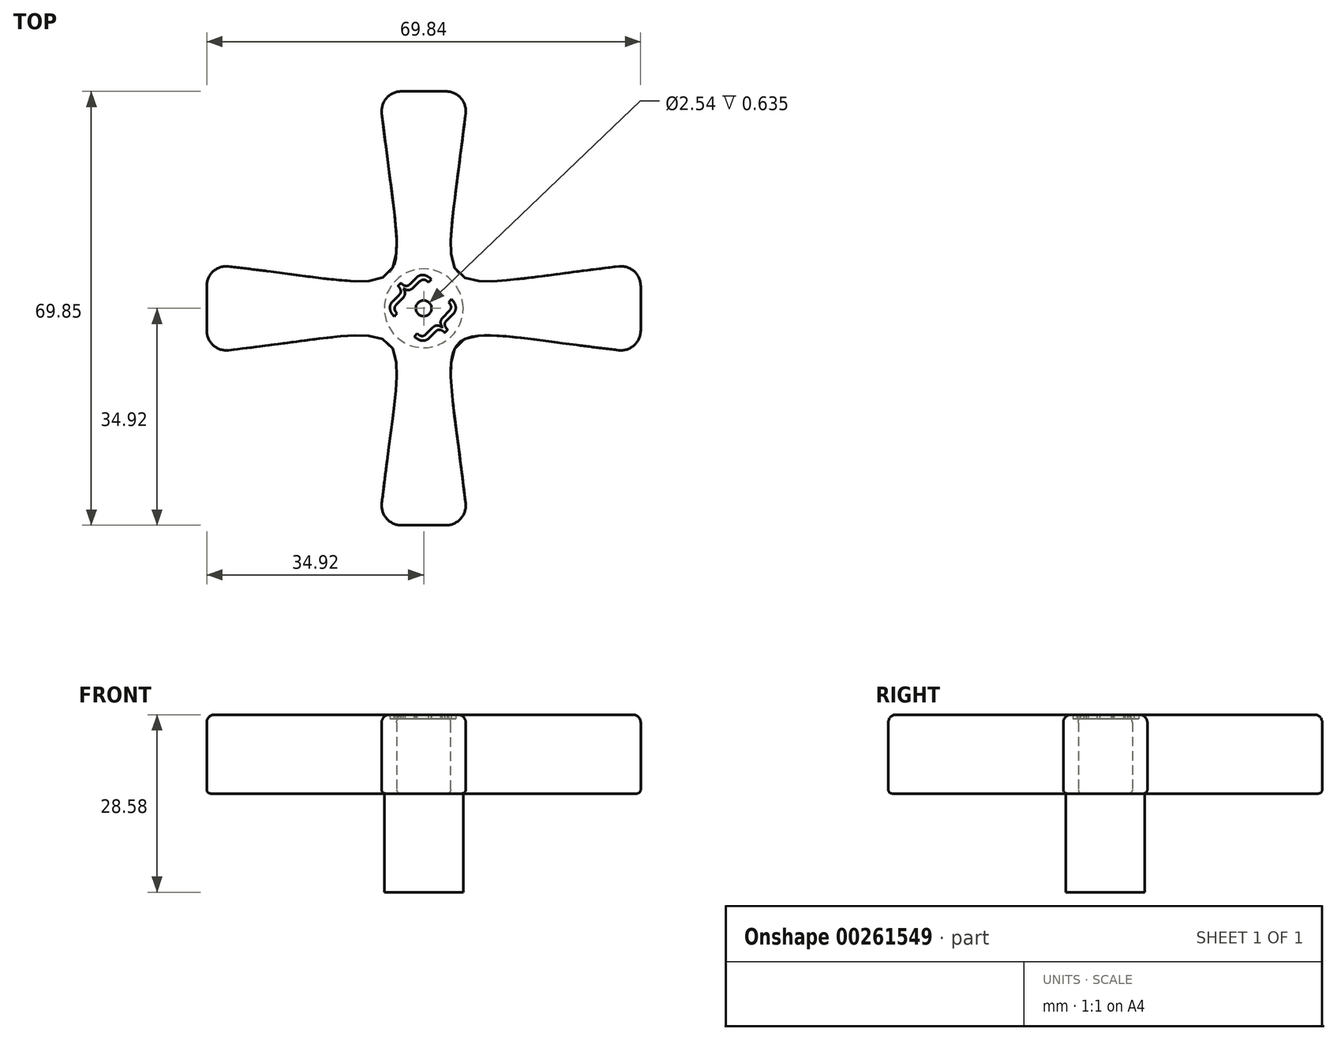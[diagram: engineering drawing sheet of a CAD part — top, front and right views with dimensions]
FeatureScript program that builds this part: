
annotation { "Feature Type Name" : "Feature", "Feature Type Description" : "" }
export const myFeature = defineFeature(function(context is Context, id is Id, definition is map)
    precondition{}
    {
        {
            var Q0;
            Q0=qCreatedBy(makeId("Top.planeOp"),FACE);
            var sketch = newSketch(context, id + "F0", { "sketchPlane" : qUnion([Q0])});
            skLineSegment(sketch, "E0", {"start": v(0, 0) * mm, "end": v(0, 34.93) * mm, "construction": true});
            skLineSegment(sketch, "E1", {"start": v(-34.92, 0) * mm, "end": v(0, 0) * mm, "construction": true});
            skLineSegment(sketch, "E2", {"start": v(34.93, 0) * mm, "end": v(0, 0) * mm, "construction": true});
            skLineSegment(sketch, "E3", {"start": v(0, -34.93) * mm, "end": v(0, 0) * mm, "construction": true});
            skLineSegment(sketch, "E4", {"start": v(-34.93, 7.14) * mm, "end": v(-34.93, -7.14) * mm});
            skLineSegment(sketch, "E5", {"start": v(-7.14, -34.93) * mm, "end": v(7.14, -34.93) * mm});
            skLineSegment(sketch, "E6", {"start": v(34.93, -7.14) * mm, "end": v(34.93, 7.14) * mm});
            skLineSegment(sketch, "E7", {"start": v(-7.14, 34.93) * mm, "end": v(7.14, 34.93) * mm});
            skCircle(sketch, "E8", {"center": v(0, 0) * mm, "radius": 15.88 * mm, "construction": true});
            skLineSegment(sketch, "E9", {"start": v(-15.88, 5.08) * mm, "end": v(-15.88, -5.08) * mm, "construction": true});
            skCircle(sketch, "E10", {"center": v(0, 0) * mm, "radius": 7.94 * mm, "construction": true});
            skLineSegment(sketch, "E11", {"start": v(-5.08, -15.88) * mm, "end": v(5.08, -15.88) * mm, "construction": true});
            skLineSegment(sketch, "E12.MirrorCS", {"start": v(0, 0) * mm, "end": v(0, -34.93) * mm, "construction": true});
            skLineSegment(sketch, "E13", {"start": v(-5.61, -5.61) * mm, "end": v(5.61, 5.61) * mm, "construction": true});
            skFitSpline(sketch, "E14", {"points": [v(-34.93, -7.14) * mm, v(-5.61, -5.61) * mm, v(-7.14, -34.93) * mm], "startDerivative": vector(114.3, 12.38) * mm, "endDerivative": vector(-12.38, -114.3) * mm});
            skFitSpline(sketch, "E15.MirrorCS", {"points": [v(34.93, -7.14) * mm, v(5.61, -5.61) * mm, v(7.14, -34.93) * mm], "startDerivative": vector(-114.3, 12.38) * mm, "endDerivative": vector(12.38, -114.3) * mm});
            skFitSpline(sketch, "E16.MirrorCS", {"points": [v(-34.93, 7.14) * mm, v(-5.61, 5.61) * mm, v(-7.14, 34.93) * mm], "startDerivative": vector(114.3, -12.38) * mm, "endDerivative": vector(-12.38, 114.3) * mm});
            skFitSpline(sketch, "E17.MirrorCS", {"points": [v(34.93, 7.14) * mm, v(5.61, 5.61) * mm, v(7.14, 34.93) * mm], "startDerivative": vector(-114.3, -12.38) * mm, "endDerivative": vector(12.38, 114.3) * mm});
            skSolve(sketch);
        }
        {
            var Q0;
            Q0=qSketchRegion(id+"F0",true);
            extrude(context, id + "F1", {"entities" : qUnion([Q0]), "depth" : 12.7 * mm});
        }
        {
            var Q0;
            Q0=makeQuery(id+"F1.opExtrude","CAP_FACE",FACE,{"disambiguationData":[OSD([sQuery(id+"F0.wireOp",EDGE,"E4"),sQuery(id+"F0.wireOp",EDGE,"E5"),sQuery(id+"F0.wireOp",EDGE,"E6"),sQuery(id+"F0.wireOp",EDGE,"E7"),sQuery(id+"F0.wireOp",EDGE,"E14"),sQuery(id+"F0.wireOp",EDGE,"E15.MirrorCS"),sQuery(id+"F0.wireOp",EDGE,"E16.MirrorCS"),sQuery(id+"F0.wireOp",EDGE,"E17.MirrorCS")])],"isStart":true});
            var sketch = newSketch(context, id + "F2", { "sketchPlane" : qUnion([Q0])});
            skCircle(sketch, "E18", {"center": v(0, 0) * mm, "radius": 6.35 * mm});
            skSolve(sketch);
        }
        {
            var Q0;
            Q0=qSketchRegion(id+"F2",true);
            extrude(context, id + "F3", {"entities" : qUnion([Q0]), "operationType" : NewBodyOperationType.ADD, "depth" : 15.88 * mm});
        }
        {
            var Q0;
            Q0=makeQuery(id+"FHBKJaG82kfliYF_1.boolean.opBoolean","MERGE",FACE,{"derivedFrom":[makeQuery(id+"F1.opExtrude","CAP_FACE",FACE,{"disambiguationData":[OSD([sQuery(id+"F0.wireOp",EDGE,"E4"),sQuery(id+"F0.wireOp",EDGE,"E5"),sQuery(id+"F0.wireOp",EDGE,"E6"),sQuery(id+"F0.wireOp",EDGE,"E7"),sQuery(id+"F0.wireOp",EDGE,"E14"),sQuery(id+"F0.wireOp",EDGE,"E15.MirrorCS"),sQuery(id+"F0.wireOp",EDGE,"E16.MirrorCS"),sQuery(id+"F0.wireOp",EDGE,"E17.MirrorCS")])],"isStart":false}),makeQuery(id+"FHBKJaG82kfliYF_1.opExtrude","CAP_FACE",FACE,{"disambiguationData":[OSD([sQuery(id+"FlcRGu9XOME26Uw_1.wireOp",EDGE,"4aeb7ee9-712b-4c87-8b6b-3736a43f95a2"),sQuery(id+"FlcRGu9XOME26Uw_1.wireOp",EDGE,"5124bdd7-5500-46ca-ada0-c6f18179f70a0.MirrorCS"),sQuery(id+"FlcRGu9XOME26Uw_1.wireOp",EDGE,"3c1a6850-1179-4b00-b570-ccdac5f7884b0.MirrorCS"),sQuery(id+"FlcRGu9XOME26Uw_1.wireOp",EDGE,"ff6566bc-f724-427d-8e95-42f8fa4ef3770.MirrorCS"),sQuery(id+"FlcRGu9XOME26Uw_1.wireOp",EDGE,"qXK4DlwG-7KnT-G8Oz-TqMb-Z13vw5oB3guk"),sQuery(id+"FlcRGu9XOME26Uw_1.wireOp",EDGE,"dqaNWhFM-M3ve-srLk-W5Z1-zQcwXBHqWryK"),sQuery(id+"FlcRGu9XOME26Uw_1.wireOp",EDGE,"r9uwT2Yu-TUu2-pDg3-xqRF-IJZkSwj9vNKo"),sQuery(id+"FlcRGu9XOME26Uw_1.wireOp",EDGE,"dcotBPHB-oE0p-CpJw-bHCk-VDZde19CIVf2")])],"isStart":true})]});
            var sketch = newSketch(context, id + "F4", { "sketchPlane" : qUnion([Q0])});
            skText(sketch, "E19", { "text": "{", "fontName": "OpenSans-Regular.ttf"});
            skText(sketch, "E20", { "text": "}", "fontName": "OpenSans-Regular.ttf"});
            skLineSegment(sketch, "E21", {"start": v(-3.2, -0.67) * mm, "end": v(-0.67, -3.2) * mm, "construction": true});
            skLineSegment(sketch, "E22", {"start": v(-1.94, -1.94) * mm, "end": v(9.49, 9.49) * mm, "construction": true});
            skLineSegment(sketch, "E23", {"start": v(-3.27, 3.18) * mm, "end": v(2.64, -2.74) * mm, "construction": true});
            skCircle(sketch, "E24", {"center": v(0, 0) * mm, "radius": 1.27 * mm});
            const initialGuessF4  = {"E19": [-0.00602, 0.00214, 0.7071, -0.7071, 0.00698], "E20": [-0.00067, -0.0032, 0.7071, -0.7071, 0.00699]};
            skSetInitialGuess(sketch, initialGuessF4);
            skSolve(sketch);
        }
        {
            var Q0;
            Q0=qSketchRegion(id+"F4",true);
            extrude(context, id + "F5", {"entities" : qUnion([Q0]), "operationType" : NewBodyOperationType.REMOVE, "oppositeDirection" : true, "depth" : 0.64 * mm});
        }
        {
            var Q0;
            Q0=makeQuery(id+"F1.opExtrude","SWEPT_EDGE",EDGE,{"disambiguationData":[OSD([sQuery(id+"F0.wireOp",EDGE,"E5"),sQuery(id+"F0.wireOp",EDGE,"E15.MirrorCS")])]});
            var Q1;
            Q1=makeQuery(id+"F1.opExtrude","SWEPT_EDGE",EDGE,{"disambiguationData":[OSD([sQuery(id+"F0.wireOp",EDGE,"E6"),sQuery(id+"F0.wireOp",EDGE,"E15.MirrorCS")])]});
            var Q2;
            Q2=makeQuery(id+"F1.opExtrude","SWEPT_EDGE",EDGE,{"disambiguationData":[OSD([sQuery(id+"F0.wireOp",EDGE,"E6"),sQuery(id+"F0.wireOp",EDGE,"E17.MirrorCS")])]});
            var Q3;
            Q3=makeQuery(id+"F1.opExtrude","SWEPT_EDGE",EDGE,{"disambiguationData":[OSD([sQuery(id+"F0.wireOp",EDGE,"E7"),sQuery(id+"F0.wireOp",EDGE,"E17.MirrorCS")])]});
            var Q4;
            Q4=makeQuery(id+"F1.opExtrude","SWEPT_EDGE",EDGE,{"disambiguationData":[OSD([sQuery(id+"F0.wireOp",EDGE,"E7"),sQuery(id+"F0.wireOp",EDGE,"E16.MirrorCS")])]});
            var Q5;
            Q5=makeQuery(id+"F1.opExtrude","SWEPT_EDGE",EDGE,{"disambiguationData":[OSD([sQuery(id+"F0.wireOp",EDGE,"E4"),sQuery(id+"F0.wireOp",EDGE,"E14")])]});
            var Q6;
            Q6=makeQuery(id+"F1.opExtrude","SWEPT_EDGE",EDGE,{"disambiguationData":[OSD([sQuery(id+"F0.wireOp",EDGE,"E4"),sQuery(id+"F0.wireOp",EDGE,"E16.MirrorCS")])]});
            var Q7;
            Q7=makeQuery(id+"F1.opExtrude","SWEPT_EDGE",EDGE,{"disambiguationData":[OSD([sQuery(id+"F0.wireOp",EDGE,"E5"),sQuery(id+"F0.wireOp",EDGE,"E14")])]});
            fillet(context, id + "F6", {"entities" : qUnion([Q0, Q1, Q2, Q3, Q4, Q5, Q6, Q7]), "radius" : 3.17 * mm, "tangentPropagation" : true, "allowEdgeOverflow" : false});
        }
        {
            var Q0;
            Q0=makeQuery(id+"F1.opExtrude","CAP_EDGE",EDGE,{"disambiguationData":[OSD([sQuery(id+"F0.wireOp",EDGE,"E14")])],"isStart":false});
            fillet(context, id + "F7", {"entities" : qUnion([Q0]), "radius" : 1.27 * mm, "tangentPropagation" : true, "allowEdgeOverflow" : false});
        }
        {
            var Q0;
            Q0=makeQuery(id+"F1.opExtrude","CAP_EDGE",EDGE,{"disambiguationData":[OSD([sQuery(id+"F0.wireOp",EDGE,"E16.MirrorCS")])],"isStart":true});
            fillet(context, id + "F8", {"entities" : qUnion([Q0]), "radius" : 0.64 * mm, "tangentPropagation" : true, "allowEdgeOverflow" : false});
        }
    });
